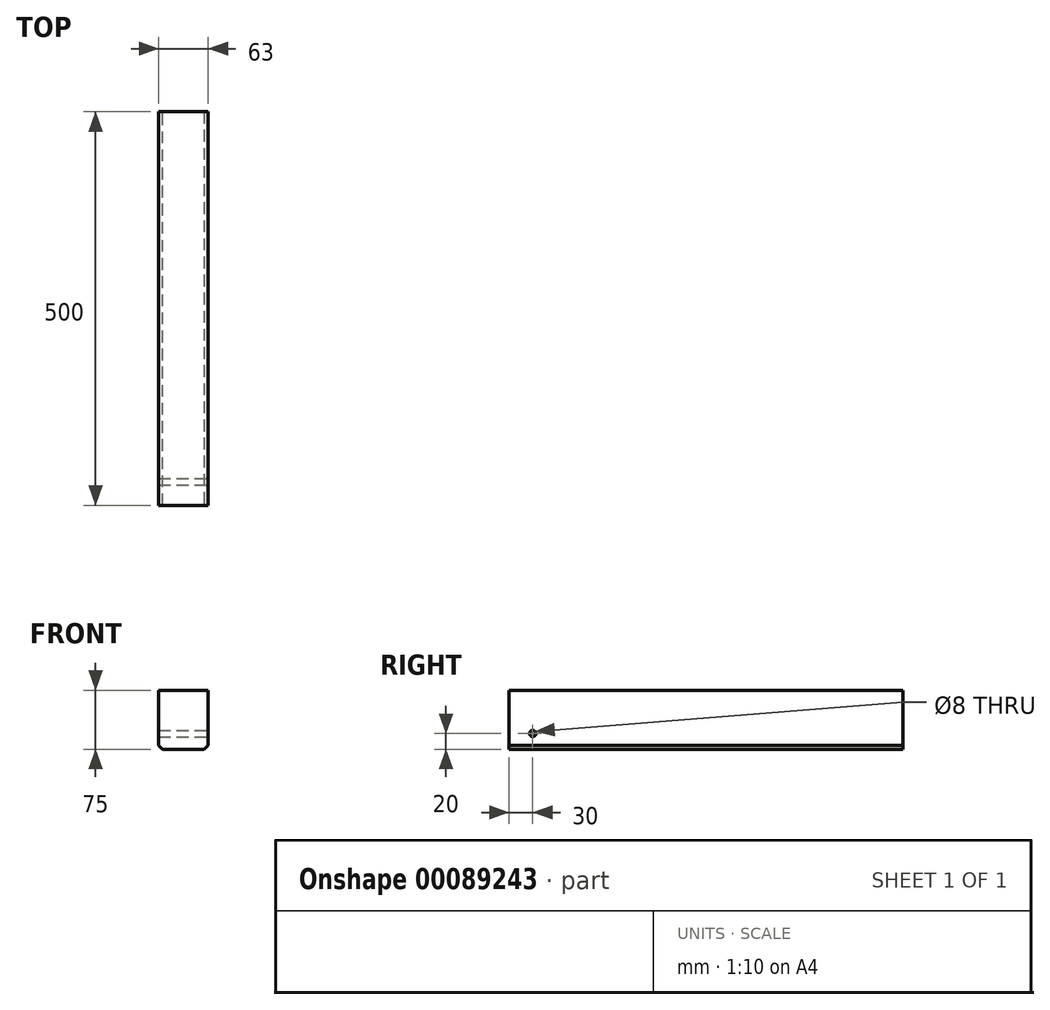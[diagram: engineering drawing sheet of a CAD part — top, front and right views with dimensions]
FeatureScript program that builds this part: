
annotation { "Feature Type Name" : "Feature", "Feature Type Description" : "" }
export const myFeature = defineFeature(function(context is Context, id is Id, definition is map)
    precondition{}
    {
        {
            var Q0;
            Q0=qCreatedBy(makeId("Front.planeOp"),FACE);
            var sketch = newSketch(context, id + "F0", { "sketchPlane" : qUnion([Q0])});
            skLineSegment(sketch, "E0.bottom", {"start": v(-31.5, 37.5) * mm, "end": v(31.5, 37.5) * mm});
            skLineSegment(sketch, "E0.top", {"start": v(-31.5, -37.5) * mm, "end": v(31.5, -37.5) * mm});
            skLineSegment(sketch, "E0.left", {"start": v(-31.5, 37.5) * mm, "end": v(-31.5, -37.5) * mm});
            skLineSegment(sketch, "E0.right", {"start": v(31.5, 37.5) * mm, "end": v(31.5, -37.5) * mm});
            skPoint(sketch, "E0.middle", {"position": v(0, 0) * mm});
            skSolve(sketch);
        }
        {
            var Q0;
            Q0=makeQuery(id+"F0.imprint","IMPRINT",FACE,{"disambiguationData":[TD([[makeQuery(id+"F0.imprint","IMPRINT",EDGE,{"derivedFrom":sQuery(id+"F0.wireOp",EDGE,"E0.bottom")}),-1.0]])]});
            extrude(context, id + "F1", {"entities" : qUnion([Q0]), "depth" : 500 * mm});
        }
        {
            var Q0;
            Q0=makeQuery(id+"F1.opExtrude","SWEPT_EDGE",EDGE,{"disambiguationData":[OSD([sQuery(id+"F0.wireOp",EDGE,"E0.top"),sQuery(id+"F0.wireOp",EDGE,"E0.right")])]});
            var Q1;
            Q1=makeQuery(id+"F1.opExtrude","SWEPT_EDGE",EDGE,{"disambiguationData":[OSD([sQuery(id+"F0.wireOp",EDGE,"E0.top"),sQuery(id+"F0.wireOp",EDGE,"E0.left")])]});
            chamfer(context, id + "F2", {"entities" : qUnion([Q0, Q1]), "width" : 5 * mm, "tangentPropagation" : true});
        }
        {
            var Q0;
            Q0=makeQuery(id+"F1.opExtrude","SWEPT_FACE",FACE,{"disambiguationData":[OSD([sQuery(id+"F0.wireOp",EDGE,"E0.right")])]});
            var sketch = newSketch(context, id + "F3", { "sketchPlane" : qUnion([Q0])});
            skCircle(sketch, "E1", {"center": v(-470, -17.5) * mm, "radius": 4 * mm});
            skSolve(sketch);
        }
        {
            var Q0;
            Q0=makeQuery(id+"F3.imprint","IMPRINT",FACE,{"disambiguationData":[TD([[makeQuery(id+"F3.imprint","IMPRINT",EDGE,{"derivedFrom":sQuery(id+"F3.wireOp",EDGE,"E1")}),1.0]])]});
            extrude(context, id + "F4", {"entities" : qUnion([Q0]), "operationType" : NewBodyOperationType.REMOVE, "endBound" : BoundingType.THROUGH_ALL, "oppositeDirection" : true, "depth" : 25 * mm});
        }
    });
